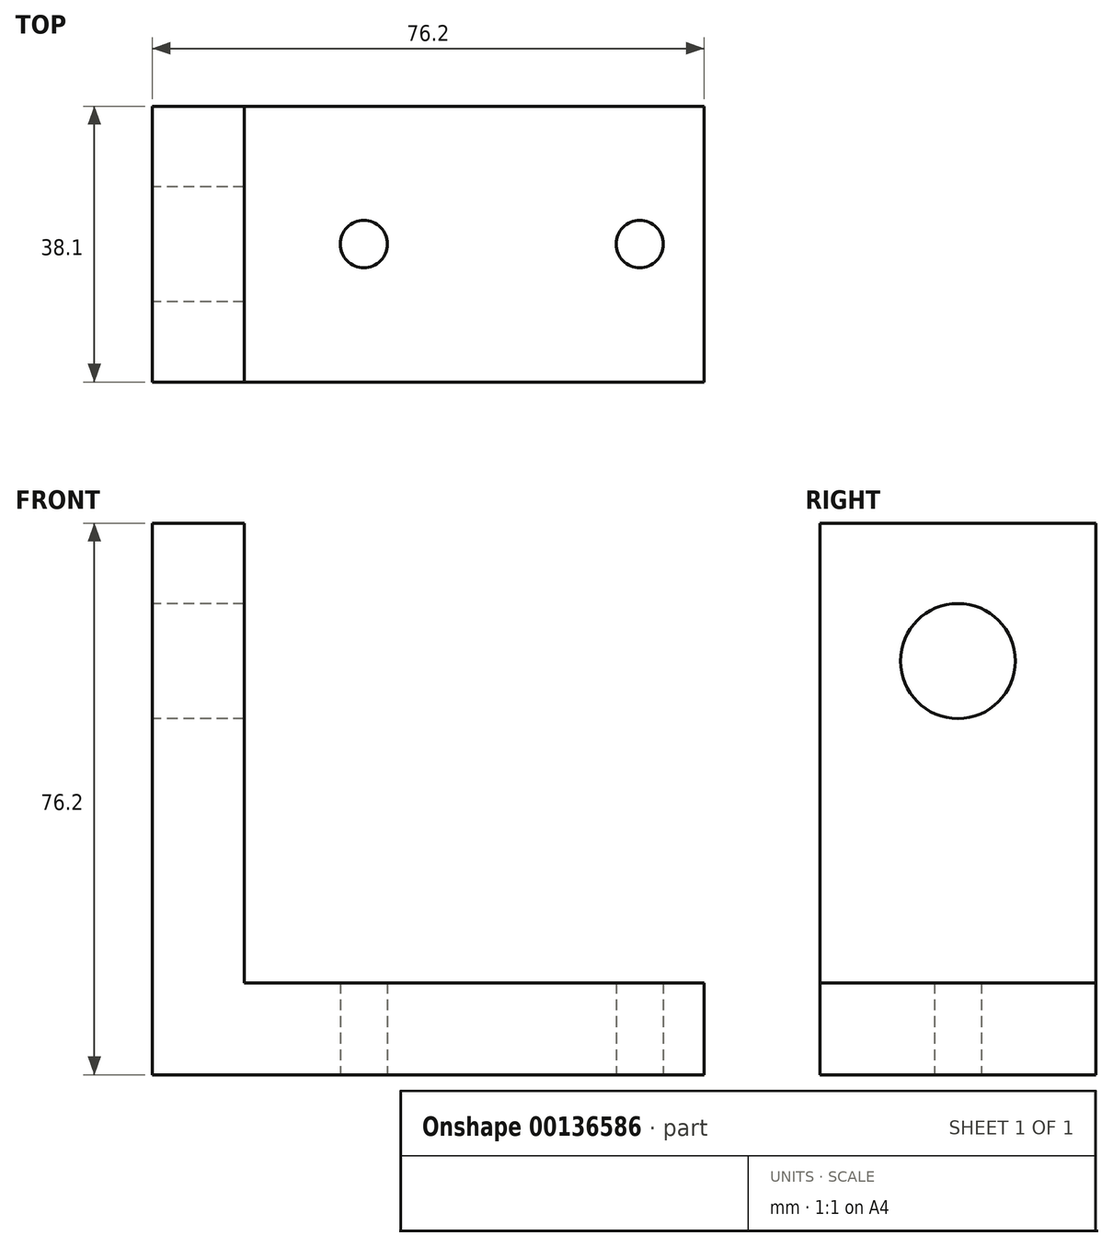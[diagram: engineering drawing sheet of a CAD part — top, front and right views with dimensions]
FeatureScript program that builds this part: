
annotation { "Feature Type Name" : "Feature", "Feature Type Description" : "" }
export const myFeature = defineFeature(function(context is Context, id is Id, definition is map)
    precondition{}
    {
        {
            var Q0;
            Q0=qCreatedBy(makeId("Top.planeOp"),FACE);
            var sketch = newSketch(context, id + "F0", { "sketchPlane" : qUnion([Q0])});
            skLineSegment(sketch, "E0.bottom", {"start": v(0, 0) * mm, "end": v(76.2, 0) * mm});
            skLineSegment(sketch, "E0.top", {"start": v(0, 38.1) * mm, "end": v(76.2, 38.1) * mm});
            skLineSegment(sketch, "E0.left", {"start": v(0, 0) * mm, "end": v(0, 38.1) * mm});
            skLineSegment(sketch, "E0.right", {"start": v(76.2, 0) * mm, "end": v(76.2, 38.1) * mm});
            skSolve(sketch);
        }
        {
            var Q0;
            Q0=makeQuery(id+"F0.imprint","IMPRINT",FACE,{"disambiguationData":[TD([[makeQuery(id+"F0.imprint","IMPRINT",EDGE,{"derivedFrom":sQuery(id+"F0.wireOp",EDGE,"E0.bottom")}),1.0]])]});
            extrude(context, id + "F1", {"entities" : qUnion([Q0]), "depth" : 12.7 * mm});
        }
        {
            var Q0;
            Q0=makeQuery(id+"F1.opExtrude","CAP_FACE",FACE,{"disambiguationData":[OSD([sQuery(id+"F0.wireOp",EDGE,"E0.bottom"),sQuery(id+"F0.wireOp",EDGE,"E0.top"),sQuery(id+"F0.wireOp",EDGE,"E0.left"),sQuery(id+"F0.wireOp",EDGE,"E0.right")])],"isStart":false});
            var sketch = newSketch(context, id + "F2", { "sketchPlane" : qUnion([Q0])});
            skLineSegment(sketch, "E1.bottom", {"start": v(0, 0) * mm, "end": v(12.7, 0) * mm});
            skLineSegment(sketch, "E1.top", {"start": v(0, 38.1) * mm, "end": v(12.7, 38.1) * mm});
            skLineSegment(sketch, "E1.left", {"start": v(0, 0) * mm, "end": v(0, 38.1) * mm});
            skLineSegment(sketch, "E1.right", {"start": v(12.7, 0) * mm, "end": v(12.7, 38.1) * mm});
            skSolve(sketch);
        }
        {
            var Q0;
            Q0=makeQuery(id+"F2.imprint","IMPRINT",FACE,{"disambiguationData":[TD([[makeQuery(id+"F2.imprint","IMPRINT",EDGE,{"derivedFrom":sQuery(id+"F2.wireOp",EDGE,"E1.bottom")}),1.0]])]});
            extrude(context, id + "F3", {"entities" : qUnion([Q0]), "operationType" : NewBodyOperationType.ADD, "depth" : 63.5 * mm});
        }
        {
            var Q0;
            Q0=makeQuery(id+"F3.boolean.opBoolean","MERGE",FACE,{"derivedFrom":[makeQuery(id+"F1.opExtrude","SWEPT_FACE",FACE,{"disambiguationData":[OSD([sQuery(id+"F0.wireOp",EDGE,"E0.left")])]}),makeQuery(id+"F3.opExtrude","SWEPT_FACE",FACE,{"disambiguationData":[OSD([sQuery(id+"F2.wireOp",EDGE,"E1.left")])]})]});
            var sketch = newSketch(context, id + "F4", { "sketchPlane" : qUnion([Q0])});
            skLineSegment(sketch, "E2", {"start": v(-19.05, 0) * mm, "end": v(-19.05, 76.2) * mm, "construction": true});
            skCircle(sketch, "E3", {"center": v(-19.05, 57.15) * mm, "radius": 7.94 * mm, "construction": true});
            skSolve(sketch);
        }
        {
            var Q0;
            Q0=sQuery(id+"F4.wireOp",VERTEX,"E3.center");
            var Q1;
            Q1=makeQuery(id+"F1.opExtrude","SWEPT_BODY",BODY,{"disambiguationData":[OSD([sQuery(id+"F0.wireOp",EDGE,"E0.bottom"),sQuery(id+"F0.wireOp",EDGE,"E0.top"),sQuery(id+"F0.wireOp",EDGE,"E0.left"),sQuery(id+"F0.wireOp",EDGE,"E0.right")])]});
            hole(context, id + "F5", {"style" : HoleStyle.SIMPLE, "endStyle" : HoleEndStyle.THROUGH, "holeDiameter" : 15.88 * mm, "locations" : qUnion([Q0]), "scope" : qUnion([Q1]), "isTappedThrough" : true});
        }
        {
            var Q0;
            Q0=makeQuery(id+"F1.opExtrude","CAP_FACE",FACE,{"disambiguationData":[OSD([sQuery(id+"F0.wireOp",EDGE,"E0.bottom"),sQuery(id+"F0.wireOp",EDGE,"E0.top"),sQuery(id+"F0.wireOp",EDGE,"E0.left"),sQuery(id+"F0.wireOp",EDGE,"E0.right")])],"isStart":true});
            var sketch = newSketch(context, id + "F6", { "sketchPlane" : qUnion([Q0])});
            skLineSegment(sketch, "E4", {"start": v(0, -19.05) * mm, "end": v(76.2, -19.05) * mm, "construction": true});
            skCircle(sketch, "E5", {"center": v(67.31, -19.05) * mm, "radius": 3.26 * mm});
            skCircle(sketch, "E6", {"center": v(29.2, -19.05) * mm, "radius": 3.26 * mm});
            skSolve(sketch);
        }
        {
            var Q0;
            Q0=sQuery(id+"F6.wireOp",VERTEX,"E5.center");
            var Q1;
            Q1=sQuery(id+"F6.wireOp",VERTEX,"E6.center");
            var Q2;
            Q2=makeQuery(id+"F1.opExtrude","SWEPT_BODY",BODY,{"disambiguationData":[OSD([sQuery(id+"F0.wireOp",EDGE,"E0.bottom"),sQuery(id+"F0.wireOp",EDGE,"E0.top"),sQuery(id+"F0.wireOp",EDGE,"E0.left"),sQuery(id+"F0.wireOp",EDGE,"E0.right")])]});
            hole(context, id + "F7", {"style" : HoleStyle.SIMPLE, "endStyle" : HoleEndStyle.THROUGH, "holeDiameter" : 6.53 * mm, "locations" : qUnion([Q0, Q1]), "scope" : qUnion([Q2]), "isTappedThrough" : true});
        }
    });
